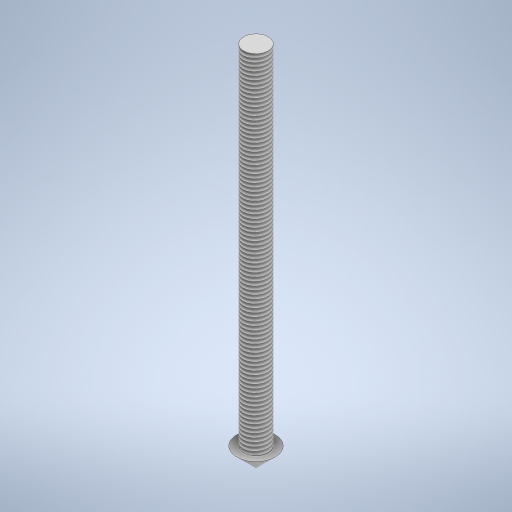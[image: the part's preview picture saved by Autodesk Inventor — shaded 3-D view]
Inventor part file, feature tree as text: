
AUTODESK INVENTOR PART (.ipt)
format: ipt  version: 2024 (Build 280153000, 153)  size: 273,920 bytes
history: native  units: mm
features: sketch x2, revolve x1, extrude x1, thread x1
ambient origin geometry x8: Origin, YZ Plane, XZ Plane, XY Plane, X Axis, Y Axis, Z Axis, Center Point
bodies: Solid1 (feature_tree)
feature tree (5):
  revolve  "Revolution1"  [1 undecoded]
  extrude  "Extrusion1"  Depth=180.0mm
  thread  "Thread1"  [1 undecoded]
  sketch  "Sketch1"  dims[d0=10.0mm d1=10.0mm]
  sketch  "Sketch2"  dims[d2=90.0deg d3=12.7mm d4=180.0mm d5=0.0mm d6=180.0mm d7=0.0mm]
note: 2 required parameter values undecoded (feature->parameter linkage not recoverable at this tier; creation-order binding heuristic only, values carry confidence <= 0.55)